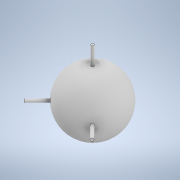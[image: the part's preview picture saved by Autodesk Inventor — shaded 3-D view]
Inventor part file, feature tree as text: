
AUTODESK INVENTOR PART (.ipt)
format: ipt  version: 2022 (Build 260153000, 153)  size: 165,376 bytes
history: native  units: in
note: dims shown in document units (in); Inventor stores cm internally (conversion verified against a paired STEP export)
features: sketch x8, extrude x6, revolve x2
ambient origin geometry x8: Origin, YZ Plane, XZ Plane, XY Plane, X Axis, Y Axis, Z Axis, Center Point
bodies: Solid1 (feature_tree)
feature tree (16):
  revolve  "Revolution1"  Angle=180.0deg
  extrude  "Extrusion1"  Depth=1.15in TaperAngle=0.0deg
  extrude  "Extrusion2"  Depth=2.5in
  extrude  "Extrusion3"  Depth=0.932in TaperAngle=0.0deg
  extrude  "Extrusion4"  Depth=0.932in TaperAngle=0.0deg
  extrude  "Extrusion5"  Depth=0.932in TaperAngle=0.0deg
  sketch  "Sketch9"  dims[d24=90.0deg d25=4.0in d26=0.0in]
  sketch  "Sketch10"
  revolve  "Revolution2"  [1 undecoded]
  extrude  "Extrusion6"  [1 undecoded]
  sketch  "Sketch1"  dims[d0=1.25in d1=180.0deg]
  sketch  "Sketch2"  dims[d2=90.0deg d3=1.5in d4=1.15in d5=0.0in d6=0.0in]
  sketch  "Sketch3"  dims[d9=1.3in d10=2.5in]
  sketch  "Sketch4"  dims[d11=4.0in d12=0.0in d16=0.932in d17=0.0in]
  sketch  "Sketch7"  dims[d18=0.125in d19=0.932in d20=0.0in]
  sketch  "Sketch8"  dims[d21=0.125in d22=0.932in d23=0.0in]
note: 2 required parameter values undecoded (feature->parameter linkage not recoverable at this tier; creation-order binding heuristic only, values carry confidence <= 0.55)